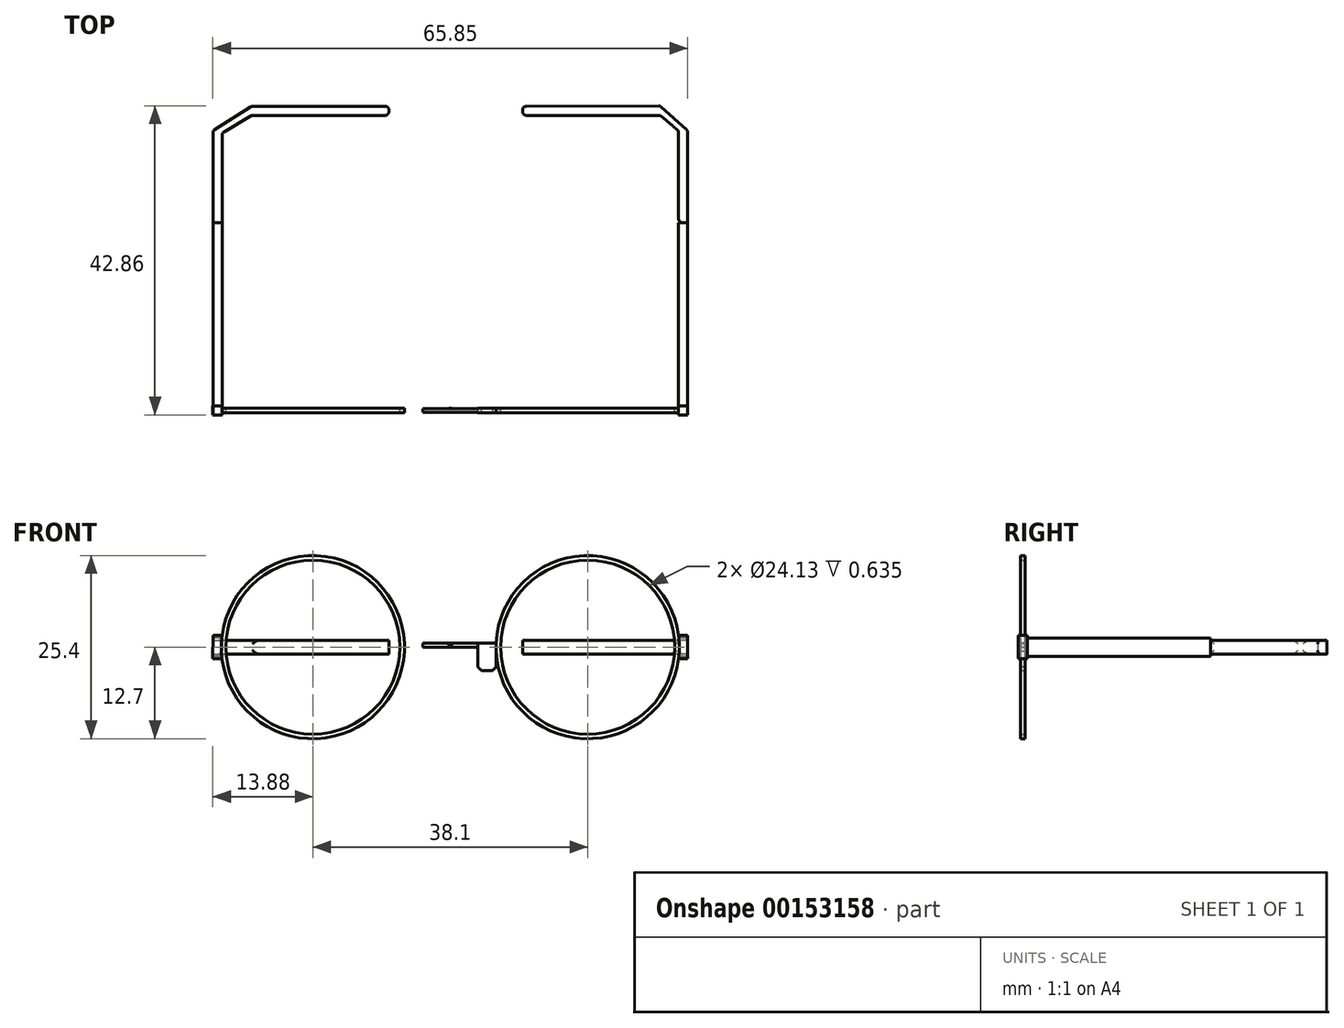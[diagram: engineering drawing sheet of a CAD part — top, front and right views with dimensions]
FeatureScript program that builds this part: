
annotation { "Feature Type Name" : "Feature", "Feature Type Description" : "" }
export const myFeature = defineFeature(function(context is Context, id is Id, definition is map)
    precondition{}
    {
        {
            var Q0;
            Q0=qCreatedBy(makeId("Front.planeOp"),FACE);
            var sketch = newSketch(context, id + "F0", { "sketchPlane" : qUnion([Q0])});
            skCircle(sketch, "E0", {"center": v(-19.05, 0) * mm, "radius": 12.7 * mm});
            skCircle(sketch, "E1", {"center": v(19.05, 0) * mm, "radius": 12.7 * mm});
            skCircle(sketch, "E2", {"center": v(-19.05, 0) * mm, "radius": 12.07 * mm});
            skCircle(sketch, "E3", {"center": v(19.05, 0) * mm, "radius": 12.07 * mm});
            skLineSegment(sketch, "E4", {"start": v(6.36, 0.56) * mm, "end": v(6.35, 0) * mm});
            skLineSegment(sketch, "E5", {"start": v(-6.35, 0) * mm, "end": v(-6.36, 0.56) * mm});
            skLineSegment(sketch, "E6.left", {"start": v(-6.36, 0.56) * mm, "end": v(-6.36, 0) * mm});
            skLineSegment(sketch, "E6.right", {"start": v(6.35, 0.56) * mm, "end": v(6.35, 0) * mm});
            skLineSegment(sketch, "E7.bottom", {"start": v(-6.36, 0.56) * mm, "end": v(6.35, 0.56) * mm});
            skLineSegment(sketch, "E7.top", {"start": v(-6.36, 0) * mm, "end": v(-6.35, 0) * mm});
            skLineSegment(sketch, "E8.bottom", {"start": v(-6.36, 0.56) * mm, "end": v(-3.82, 0.56) * mm});
            skLineSegment(sketch, "E8.top", {"start": v(-6.36, -3.25) * mm, "end": v(-3.82, -3.25) * mm});
            skLineSegment(sketch, "E8.left", {"start": v(-6.36, 0.56) * mm, "end": v(-6.36, -3.25) * mm});
            skLineSegment(sketch, "E8.right", {"start": v(-3.82, 0.56) * mm, "end": v(-3.82, -3.25) * mm});
            skLineSegment(sketch, "E9.bottom", {"start": v(6.36, 0.56) * mm, "end": v(3.82, 0.56) * mm});
            skLineSegment(sketch, "E9.top", {"start": v(6.36, -3.25) * mm, "end": v(3.82, -3.25) * mm});
            skLineSegment(sketch, "E9.left", {"start": v(6.36, 0.56) * mm, "end": v(6.36, -3.25) * mm});
            skLineSegment(sketch, "E9.right", {"start": v(3.82, 0.56) * mm, "end": v(3.82, -3.25) * mm});
            skCircle(sketch, "E10", {"center": v(0, 0.29) * mm, "radius": 0.2 * mm});
            skLineSegment(sketch, "E11.trimOffspring", {"start": v(-3.82, 0) * mm, "end": v(3.82, 0) * mm});
            skLineSegment(sketch, "E12", {"start": v(-31.65, 1.61) * mm, "end": v(-32.92, 1.61) * mm});
            skLineSegment(sketch, "E13", {"start": v(-32.92, 1.61) * mm, "end": v(-31.75, 0) * mm});
            skLineSegment(sketch, "E14", {"start": v(-31.75, 0) * mm, "end": v(-32.93, -1.59) * mm});
            skLineSegment(sketch, "E15", {"start": v(-32.93, -1.59) * mm, "end": v(-31.65, -1.59) * mm});
            skLineSegment(sketch, "E16", {"start": v(-32.92, 1.61) * mm, "end": v(-32.93, -1.59) * mm});
            skLineSegment(sketch, "E17", {"start": v(31.65, -1.59) * mm, "end": v(32.91, -1.59) * mm});
            skLineSegment(sketch, "E18", {"start": v(32.91, -1.59) * mm, "end": v(31.75, 0) * mm});
            skLineSegment(sketch, "E19", {"start": v(31.75, 0) * mm, "end": v(32.88, 1.61) * mm});
            skLineSegment(sketch, "E20", {"start": v(32.88, 1.61) * mm, "end": v(31.65, 1.61) * mm});
            skLineSegment(sketch, "E21", {"start": v(32.88, 1.61) * mm, "end": v(32.91, -1.59) * mm});
            skSolve(sketch);
        }
        {
            var Q0;
            Q0=makeQuery(id+"F0.imprint","IMPRINT",FACE,{"disambiguationData":[TD([[makeQuery(id+"F0.imprint","IMPRINT",EDGE,{"derivedFrom":sQuery(id+"F0.wireOp",EDGE,"E2")}),-1.0]])]});
            var Q1;
            Q1=makeQuery(id+"F0.imprint","IMPRINT",FACE,{"disambiguationData":[TD([[makeQuery(id+"F0.imprint","IMPRINT",EDGE,{"derivedFrom":sQuery(id+"F0.wireOp",EDGE,"E3")}),-1.0]])]});
            extrude(context, id + "F1", {"entities" : qUnion([Q0, Q1]), "endBound" : BoundingType.SYMMETRIC, "depth" : 0.64 * mm});
        }
        {
            var Q0;
            {var subQ1=sQuery(id+"F0.wireOp",EDGE,"E7.bottom");Q0=makeQuery(id+"F0.imprint","IMPRINT",FACE,{"disambiguationData":[TD([[makeQuery(id+"F0.imprint","IMPRINT",EDGE,{"derivedFrom":subQ1}),-1.0]])]});}
            extrude(context, id + "F2", {"entities" : qUnion([Q0]), "endBound" : BoundingType.SYMMETRIC, "depth" : 0.5 * mm});
        }
        {
            var Q0;
            {var subQ2=sQuery(id+"F0.wireOp",EDGE,"E8.bottom");Q0=makeQuery(id+"F0.imprint","IMPRINT",FACE,{"disambiguationData":[TD([[makeQuery(id+"F0.imprint","IMPRINT",EDGE,{"derivedFrom":subQ2}),-1.0]])]});}
            var Q1;
            {var subQ0=sQuery(id+"F0.wireOp",EDGE,"E6.right");Q1=makeQuery(id+"F0.imprint","IMPRINT",FACE,{"disambiguationData":[TD([[makeQuery(id+"F0.imprint","IMPRINT",EDGE,{"derivedFrom":subQ0}),-1.0]])]});}
            extrude(context, id + "F3", {"entities" : qUnion([Q0, Q1]), "operationType" : NewBodyOperationType.ADD, "endBound" : BoundingType.SYMMETRIC, "oppositeDirection" : true, "depth" : 0.64 * mm});
        }
        {
            var Q0;
            Q0=makeQuery(id+"F3.opExtrude","SWEPT_EDGE",EDGE,{"disambiguationData":[OSD([sQuery(id+"F0.wireOp",EDGE,"E8.top"),sQuery(id+"F0.wireOp",EDGE,"E8.left")])]});
            var Q1;
            Q1=makeQuery(id+"F3.opExtrude","SWEPT_EDGE",EDGE,{"disambiguationData":[OSD([sQuery(id+"F0.wireOp",EDGE,"E8.top"),sQuery(id+"F0.wireOp",EDGE,"E8.right")])]});
            var Q2;
            Q2=makeQuery(id+"F3.opExtrude","SWEPT_EDGE",EDGE,{"disambiguationData":[OSD([sQuery(id+"F0.wireOp",EDGE,"E9.top"),sQuery(id+"F0.wireOp",EDGE,"E9.left")])]});
            var Q3;
            Q3=makeQuery(id+"F3.opExtrude","SWEPT_EDGE",EDGE,{"disambiguationData":[OSD([sQuery(id+"F0.wireOp",EDGE,"E9.top"),sQuery(id+"F0.wireOp",EDGE,"E9.right")])]});
            chamfer(context, id + "F4", {"entities" : qUnion([Q0, Q1, Q2, Q3]), "width" : 0.5 * mm, "tangentPropagation" : true});
        }
        {
            var Q0;
            Q0=makeQuery(id+"F0.imprint","IMPRINT",FACE,{"disambiguationData":[TD([[makeQuery(id+"F0.imprint","IMPRINT",EDGE,{"derivedFrom":sQuery(id+"F0.wireOp",EDGE,"E10")}),1.0]])]});
            var Q1;
            Q1=sQuery(id+"F0.wireOp",EDGE,"E10");
            extrude(context, id + "F5", {"entities" : qUnion([Q0]), "operationType" : NewBodyOperationType.ADD, "surfaceEntities" : qUnion([Q1]), "endBound" : BoundingType.SYMMETRIC, "depth" : 0.56 * mm});
        }
        {
            var Q0;
            Q0=makeQuery(id+"F0.imprint","IMPRINT",FACE,{"disambiguationData":[TD([[makeQuery(id+"F0.imprint","IMPRINT",EDGE,{"derivedFrom":sQuery(id+"F0.wireOp",EDGE,"E13")}),-1.0]])]});
            var Q1;
            {var subQ0=sQuery(id+"F0.wireOp",EDGE,"E12");Q1=makeQuery(id+"F0.imprint","IMPRINT",FACE,{"disambiguationData":[TD([[makeQuery(id+"F0.imprint","IMPRINT",EDGE,{"derivedFrom":subQ0}),1.0]])]});}
            var Q2;
            {var subQ0=sQuery(id+"F0.wireOp",EDGE,"E14");Q2=makeQuery(id+"F0.imprint","IMPRINT",FACE,{"disambiguationData":[TD([[makeQuery(id+"F0.imprint","IMPRINT",EDGE,{"derivedFrom":subQ0}),1.0]])]});}
            var Q3;
            Q3=makeQuery(id+"F0.imprint","IMPRINT",FACE,{"disambiguationData":[TD([[makeQuery(id+"F0.imprint","IMPRINT",EDGE,{"derivedFrom":sQuery(id+"F0.wireOp",EDGE,"E18")}),-1.0]])]});
            var Q4;
            {var subQ0=sQuery(id+"F0.wireOp",EDGE,"E18");Q4=makeQuery(id+"F0.imprint","IMPRINT",FACE,{"disambiguationData":[TD([[makeQuery(id+"F0.imprint","IMPRINT",EDGE,{"derivedFrom":subQ0}),1.0]])]});}
            var Q5;
            {var subQ0=sQuery(id+"F0.wireOp",EDGE,"E19");Q5=makeQuery(id+"F0.imprint","IMPRINT",FACE,{"disambiguationData":[TD([[makeQuery(id+"F0.imprint","IMPRINT",EDGE,{"derivedFrom":subQ0}),1.0]])]});}
            extrude(context, id + "F6", {"entities" : qUnion([Q0, Q1, Q2, Q3, Q4, Q5]), "endBound" : BoundingType.SYMMETRIC, "depth" : 1.27 * mm});
        }
        {
            var Q0;
            Q0=qCreatedBy(makeId("Top.planeOp"),FACE);
            var sketch = newSketch(context, id + "F7", { "sketchPlane" : qUnion([Q0])});
            skLineSegment(sketch, "E22", {"start": v(-32.91, 0.64) * mm, "end": v(-32.91, 26.04) * mm});
            skLineSegment(sketch, "E23", {"start": v(-32.91, 26.04) * mm, "end": v(-32.91, 38.74) * mm});
            skLineSegment(sketch, "E24", {"start": v(-32.91, 38.74) * mm, "end": v(-27.57, 42.17) * mm});
            skLineSegment(sketch, "E25", {"start": v(-27.57, 42.17) * mm, "end": v(-8.52, 42.17) * mm});
            skLineSegment(sketch, "E26", {"start": v(-8.52, 42.17) * mm, "end": v(-8.52, 40.9) * mm});
            skLineSegment(sketch, "E27", {"start": v(-8.52, 40.9) * mm, "end": v(-27.57, 40.9) * mm});
            skLineSegment(sketch, "E28", {"start": v(-31.64, 26.04) * mm, "end": v(-31.64, 0.64) * mm});
            skLineSegment(sketch, "E29", {"start": v(-31.64, 0.64) * mm, "end": v(-32.91, 0.64) * mm});
            skLineSegment(sketch, "E30", {"start": v(-31.64, 26.04) * mm, "end": v(-31.64, 38.46) * mm});
            skLineSegment(sketch, "E31", {"start": v(-27.57, 40.9) * mm, "end": v(-31.64, 38.46) * mm});
            skLineSegment(sketch, "E32", {"start": v(32.92, 0.64) * mm, "end": v(32.92, 26.04) * mm});
            skLineSegment(sketch, "E33", {"start": v(32.92, 26.04) * mm, "end": v(32.92, 38.74) * mm});
            skLineSegment(sketch, "E34", {"start": v(32.92, 38.74) * mm, "end": v(29.07, 42.22) * mm});
            skLineSegment(sketch, "E35", {"start": v(29.07, 42.22) * mm, "end": v(10.02, 42.17) * mm});
            skLineSegment(sketch, "E36", {"start": v(10.02, 42.17) * mm, "end": v(10.02, 40.9) * mm});
            skLineSegment(sketch, "E37", {"start": v(10.02, 40.9) * mm, "end": v(29.07, 40.9) * mm});
            skLineSegment(sketch, "E38", {"start": v(32.92, 0.64) * mm, "end": v(31.65, 0.64) * mm});
            skLineSegment(sketch, "E39", {"start": v(31.65, 0.64) * mm, "end": v(31.65, 26.04) * mm});
            skLineSegment(sketch, "E40", {"start": v(31.65, 26.04) * mm, "end": v(31.65, 38.74) * mm});
            skLineSegment(sketch, "E41", {"start": v(29.07, 40.9) * mm, "end": v(31.65, 38.74) * mm});
            skLineSegment(sketch, "E42", {"start": v(-32.91, 26.04) * mm, "end": v(-31.64, 26.04) * mm});
            skLineSegment(sketch, "E43", {"start": v(32.92, 26.04) * mm, "end": v(31.65, 26.04) * mm});
            skSolve(sketch);
        }
        {
            var Q0;
            Q0=makeQuery(id+"F7.imprint","IMPRINT",FACE,{"disambiguationData":[TD([[makeQuery(id+"F7.imprint","IMPRINT",EDGE,{"derivedFrom":sQuery(id+"F7.wireOp",EDGE,"E22")}),-1.0]])]});
            var Q1;
            Q1=makeQuery(id+"F7.imprint","IMPRINT",FACE,{"disambiguationData":[TD([[makeQuery(id+"F7.imprint","IMPRINT",EDGE,{"derivedFrom":sQuery(id+"F7.wireOp",EDGE,"E32")}),1.0]])]});
            extrude(context, id + "F8", {"entities" : qUnion([Q0, Q1]), "endBound" : BoundingType.SYMMETRIC, "depth" : 2.54 * mm});
        }
        {
            var Q0;
            Q0=makeQuery(id+"F7.imprint","IMPRINT",FACE,{"disambiguationData":[TD([[makeQuery(id+"F7.imprint","IMPRINT",EDGE,{"derivedFrom":sQuery(id+"F7.wireOp",EDGE,"E23")}),-1.0]])]});
            var Q1;
            Q1=makeQuery(id+"F7.imprint","IMPRINT",FACE,{"disambiguationData":[TD([[makeQuery(id+"F7.imprint","IMPRINT",EDGE,{"derivedFrom":sQuery(id+"F7.wireOp",EDGE,"E33")}),1.0]])]});
            extrude(context, id + "F9", {"entities" : qUnion([Q0, Q1]), "endBound" : BoundingType.SYMMETRIC, "depth" : 1.9 * mm});
        }
        {
            var Q0;
            Q0=makeQuery(id+"F9.opExtrude","SWEPT_EDGE",EDGE,{"disambiguationData":[OSD([sQuery(id+"F7.wireOp",EDGE,"E26"),sQuery(id+"F7.wireOp",EDGE,"E27")])]});
            var Q1;
            Q1=makeQuery(id+"F9.opExtrude","SWEPT_EDGE",EDGE,{"disambiguationData":[OSD([sQuery(id+"F7.wireOp",EDGE,"E25"),sQuery(id+"F7.wireOp",EDGE,"E26")])]});
            var Q2;
            Q2=makeQuery(id+"F9.opExtrude","SWEPT_EDGE",EDGE,{"disambiguationData":[OSD([sQuery(id+"F7.wireOp",EDGE,"E35"),sQuery(id+"F7.wireOp",EDGE,"E36")])]});
            var Q3;
            Q3=makeQuery(id+"F9.opExtrude","SWEPT_EDGE",EDGE,{"disambiguationData":[OSD([sQuery(id+"F7.wireOp",EDGE,"E36"),sQuery(id+"F7.wireOp",EDGE,"E37")])]});
            var Q4;
            Q4=makeQuery(id+"F9.opExtrude","SWEPT_EDGE",EDGE,{"disambiguationData":[OSD([sQuery(id+"F7.wireOp",EDGE,"E24"),sQuery(id+"F7.wireOp",EDGE,"E25")])]});
            var Q5;
            Q5=makeQuery(id+"F9.opExtrude","SWEPT_EDGE",EDGE,{"disambiguationData":[OSD([sQuery(id+"F7.wireOp",EDGE,"E23"),sQuery(id+"F7.wireOp",EDGE,"E24")])]});
            var Q6;
            Q6=makeQuery(id+"F9.opExtrude","SWEPT_EDGE",EDGE,{"disambiguationData":[OSD([sQuery(id+"F7.wireOp",EDGE,"E34"),sQuery(id+"F7.wireOp",EDGE,"E35")])]});
            var Q7;
            Q7=makeQuery(id+"F9.opExtrude","SWEPT_EDGE",EDGE,{"disambiguationData":[OSD([sQuery(id+"F7.wireOp",EDGE,"E33"),sQuery(id+"F7.wireOp",EDGE,"E34")])]});
            var Q8;
            Q8=makeQuery(id+"F9.opExtrude","SWEPT_EDGE",EDGE,{"disambiguationData":[OSD([sQuery(id+"F7.wireOp",EDGE,"E37"),sQuery(id+"F7.wireOp",EDGE,"E41")])]});
            var Q9;
            Q9=makeQuery(id+"F9.opExtrude","SWEPT_EDGE",EDGE,{"disambiguationData":[OSD([sQuery(id+"F7.wireOp",EDGE,"E40"),sQuery(id+"F7.wireOp",EDGE,"E41")])]});
            var Q10;
            Q10=makeQuery(id+"F9.opExtrude","SWEPT_FACE",FACE,{"disambiguationData":[OSD([sQuery(id+"F7.wireOp",EDGE,"E31")])]});
            var Q11;
            Q11=makeQuery(id+"F9.opExtrude","SWEPT_FACE",FACE,{"disambiguationData":[OSD([sQuery(id+"F7.wireOp",EDGE,"E40")])]});
            fillet(context, id + "F10", {"entities" : qUnion([Q0, Q1, Q2, Q3, Q4, Q5, Q6, Q7, Q8, Q9, Q10, Q11]), "radius" : 0.5 * mm, "tangentPropagation" : true, "allowEdgeOverflow" : false});
        }
    });
